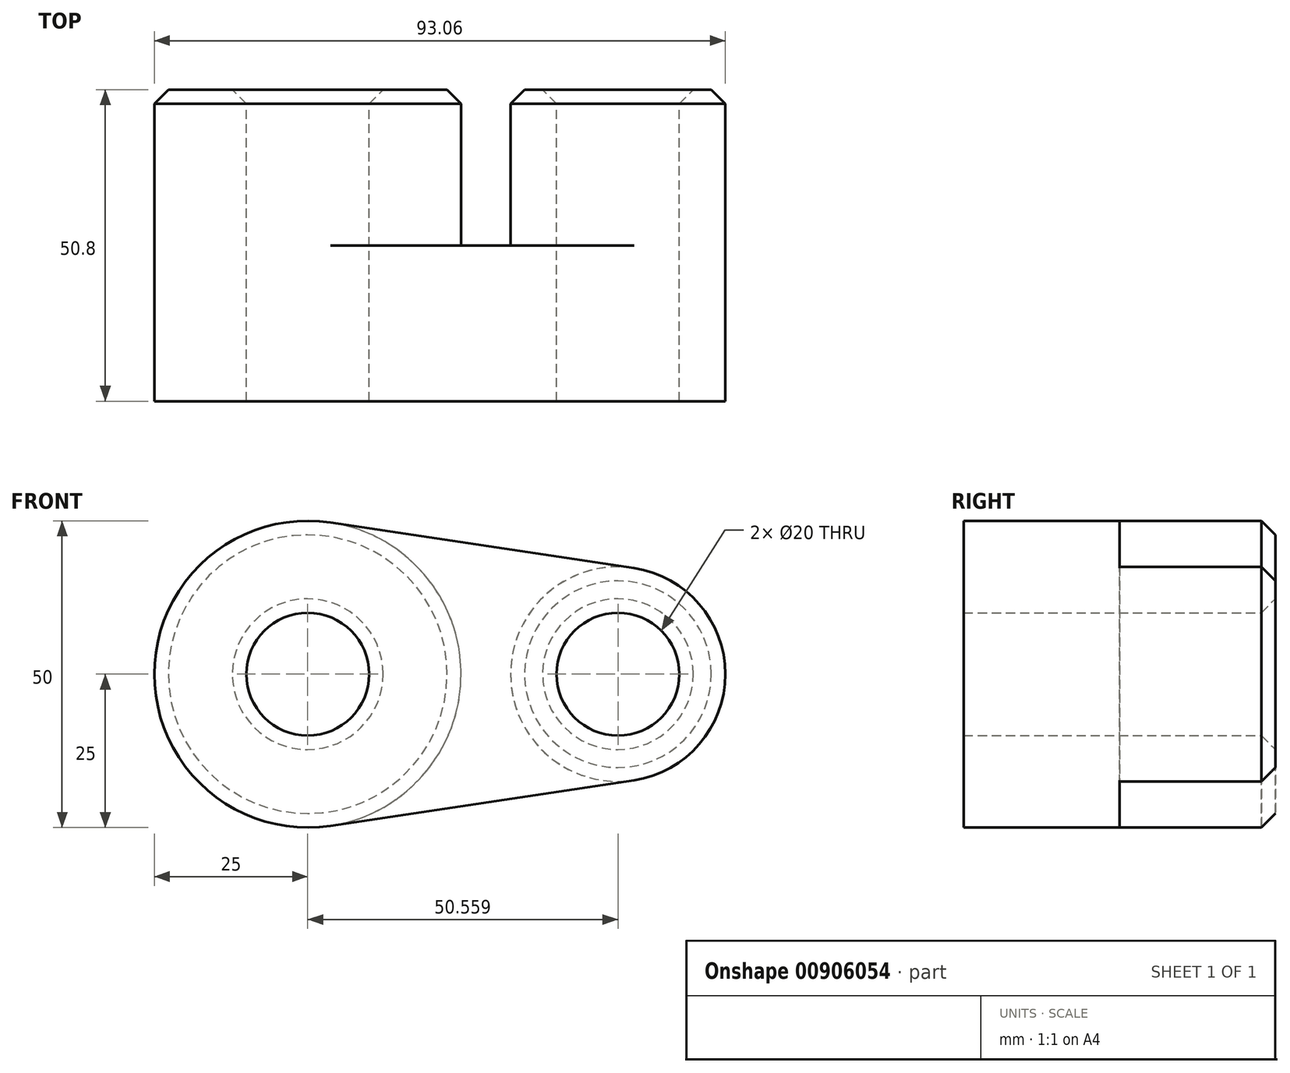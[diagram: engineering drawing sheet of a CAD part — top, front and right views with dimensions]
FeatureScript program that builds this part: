
annotation { "Feature Type Name" : "Feature", "Feature Type Description" : "" }
export const myFeature = defineFeature(function(context is Context, id is Id, definition is map)
    precondition{}
    {
        {
            var Q0;
            Q0=qCreatedBy(makeId("Front.planeOp"),FACE);
            var sketch = newSketch(context, id + "F0", { "sketchPlane" : qUnion([Q0])});
            skCircle(sketch, "E0", {"center": v(0, 0) * mm, "radius": 25 * mm});
            skCircle(sketch, "E1", {"center": v(50.56, 0) * mm, "radius": 17.5 * mm});
            skLineSegment(sketch, "E2", {"start": v(3.7, 24.72) * mm, "end": v(53.16, 17.3) * mm});
            skLineSegment(sketch, "E3", {"start": v(3.7, -24.72) * mm, "end": v(53.16, -17.3) * mm});
            skCircle(sketch, "E4", {"center": v(0, 0) * mm, "radius": 10 * mm});
            skCircle(sketch, "E5", {"center": v(50.56, 0) * mm, "radius": 10 * mm});
            skSolve(sketch);
        }
        {
            var Q0;
            Q0 = qSketchRegion(id + "F0", true);
            extrude(context, id + "F1", {"entities" : qUnion([Q0]), "depth" : 25.4 * mm, "offsetDistance" : 25.4 * mm});
        }
        {
            var Q0;
            Q0=sQuery(id+"F0.wireOp",EDGE,"E4");
            extrude(context, id + "F2", {"bodyType" : ToolBodyType.SURFACE, "surfaceEntities" : qUnion([Q0]), "depth" : 25.4 * mm, "offsetDistance" : 25.4 * mm});
        }
        {
            var Q0;
            Q0=makeQuery(id+"F0.imprint","IMPRINT",FACE,{"disambiguationData":[TD([[makeQuery(id+"F0.imprint","IMPRINT",EDGE,{"derivedFrom":sQuery(id+"F0.wireOp",EDGE,"E4")}),-1.0]])]});
            var Q1;
            Q1=makeQuery(id+"F0.imprint","IMPRINT",FACE,{"disambiguationData":[TD([[makeQuery(id+"F0.imprint","IMPRINT",EDGE,{"derivedFrom":sQuery(id+"F0.wireOp",EDGE,"E5")}),-1.0]])]});
            extrude(context, id + "F3", {"entities" : qUnion([Q0, Q1]), "operationType" : NewBodyOperationType.ADD, "depth" : 25.4 * mm, "offsetDistance" : 25.4 * mm});
        }
        {
            var Q0;
            Q0=makeQuery(id+"F0.imprint","IMPRINT",FACE,{"disambiguationData":[TD([[makeQuery(id+"F0.imprint","IMPRINT",EDGE,{"derivedFrom":sQuery(id+"F0.wireOp",EDGE,"E4")}),-1.0]])]});
            var Q1;
            Q1=makeQuery(id+"F0.imprint","IMPRINT",FACE,{"disambiguationData":[TD([[makeQuery(id+"F0.imprint","IMPRINT",EDGE,{"derivedFrom":sQuery(id+"F0.wireOp",EDGE,"E5")}),-1.0]])]});
            extrude(context, id + "F4", {"entities" : qUnion([Q0, Q1]), "operationType" : NewBodyOperationType.ADD, "oppositeDirection" : true, "depth" : 25.4 * mm, "offsetDistance" : 25.4 * mm});
        }
        {
            var Q0;
            Q0=makeQuery(id+"F4.opExtrude","CAP_EDGE",EDGE,{"disambiguationData":[OSD([sQuery(id+"F0.wireOp",EDGE,"E4")])],"isStart":false});
            var Q1;
            Q1=makeQuery(id+"F4.opExtrude","CAP_EDGE",EDGE,{"disambiguationData":[OSD([sQuery(id+"F0.wireOp",EDGE,"E0")])],"isStart":false});
            var Q2;
            Q2=makeQuery(id+"F4.opExtrude","CAP_EDGE",EDGE,{"disambiguationData":[OSD([sQuery(id+"F0.wireOp",EDGE,"E1")])],"isStart":false});
            var Q3;
            Q3=makeQuery(id+"F4.opExtrude","CAP_EDGE",EDGE,{"disambiguationData":[OSD([sQuery(id+"F0.wireOp",EDGE,"E5")])],"isStart":false});
            chamfer(context, id + "F5", {"entities" : qUnion([Q0, Q1, Q2, Q3]), "width" : 2.3 * mm, "tangentPropagation" : true});
        }
    });
